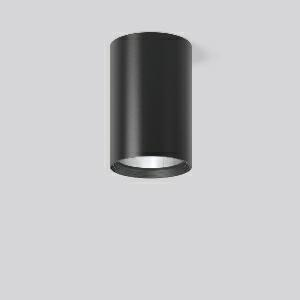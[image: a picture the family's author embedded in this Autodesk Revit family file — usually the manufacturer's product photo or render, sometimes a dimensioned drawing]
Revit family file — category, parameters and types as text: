
# Revit family: heledon_maxi_a_931218_003_e7fa
name_source: partatom
category: Lighting Fixtures
units: mm (PartAtom-declared; Revit-internal decimal feet)

## family parameters
Cut with Voids When Loaded = No
Host = Face
Light Source = No
Part Type = Normal
Room Calculation Point = No
Round Connector Dimension = Use Diameter
Shared = No

## types (1)
- HELEDON maxi A (1 x LED Modul 930, 3350 lm, 3000)
    Apparent Load = 25 VA
    Approval mark = CE
    CIE Flux Codes = 100 100 100 100 100
    Color Rendering = 90
    Color Temperature = 3000
    Default Elevation = 1800 mm
    Description = Series: HELEDON maxi
Cylindrical surface-mounted downlight. Housing: die-cast aluminium, powder-coated. Internal ceiling frame polycarbonate with bayonet mounting. Black plastic ring and recessed LED to prevent glare from the side. Optical assembly with reflector made of MIRO-Silver with 98% total light reflection for outstanding efficiency - can be changed without tools. Best colour rendering index Ra>90. Suitable for Ceiling mounting. Easy installation with a separate ceiling frame with bayonet mounting and plug connection. Driver integrated. Connected via plug-in connector. High quality converter without flickering and stroboscopic effect. The following accessories can be mounted without use of tools: interchangeable lenses, decorative glasses, honeycomb louvre, clear and frosted diffusers, white interchangeable plastic ring. 
Colour: deep black, matt (RAL 9005)
Diameter: 123 mm
Height: 183 mm
Lamp: LED
Socket: without socket
Colour temperature: 3000K
Colour rendering index (CRI): 92
System power: 25 W
Rated luminous flux: 3350 lm
Luminous efficiency: 134 lm/W
Control gear: Regulated power supply
Protection class: I
Type of protection: IP 20
    Height = 183 mm
    Lamp = 1 x LED Modul 930
    Lamp Light Flux = 3350 lm
    Lamp count = 1
    Length = 123 mm
    Lifetime = 50000 h
    Luminous efficacy = 134 lm/W
    Manufacturer = RZB
    ModVariant = No
    Model = 931218.003
    Mounting Place = Ceiling
    Mounting Type = Surface mounted
    Number of Poles = 1
    OnlyDefault = Yes
    Power Factor = 1
    Product Name = HELEDON maxi A
    Product group = Surface mounted downlights
    ProductGroupID = 302
    Protection Class = Protection class I
    Protection Degree = IP 20
    RLX_Detail_Level = 1
    RLX_Emergency_Light_Flux = 0 lm
    RLX_Emergency_Type = 0
    RLX_Emergency_Type_DB = No
    RlxData = <blob elided: 97745 chars, md5=823a74c3>
    Socket = socket
    Standby Power = 0 W
    System Light Flux = 3350 lm
    System Power = 25 W
    Type Comments = Product without accessories
    Type Image = 931192.003.jpg
    URL = http://relux.com
    VarID = ---
    Voltage = 230 V
    Voltage Range = 220-240 V
    Weight = 0.00 kg
    Width = 0 mm  [stored 0 ft]

note: [stored X ft] marks values corroborated as IEEE doubles in the binary element streams (Revit-internal decimal feet)

## geometry (parser evidence)
native form markers: Blend x4, Sweep x11
no freeform markers — native parametric forms only
